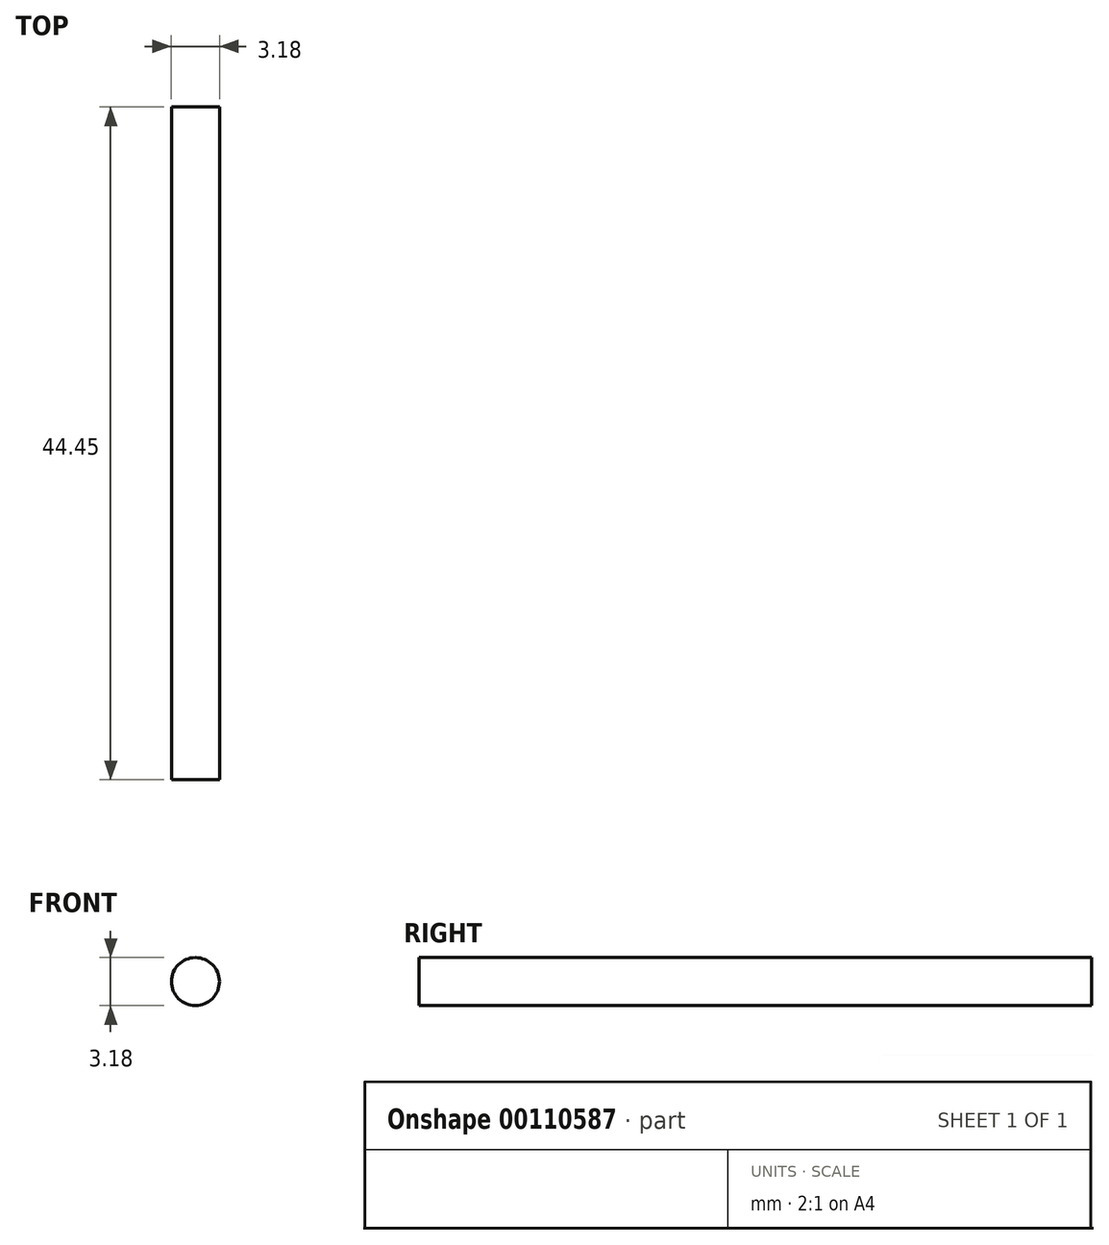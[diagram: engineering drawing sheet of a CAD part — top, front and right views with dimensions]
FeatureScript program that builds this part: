
annotation { "Feature Type Name" : "Feature", "Feature Type Description" : "" }
export const myFeature = defineFeature(function(context is Context, id is Id, definition is map)
    precondition{}
    {
        {
            var Q0;
            Q0=qCreatedBy(makeId("Front.planeOp"),FACE);
            var sketch = newSketch(context, id + "F0", { "sketchPlane" : qUnion([Q0])});
            skCircle(sketch, "E0", {"center": v(0, 0) * mm, "radius": 1.59 * mm});
            skSolve(sketch);
        }
        {
            var Q0;
            Q0=makeQuery(id+"F0.imprint","IMPRINT",FACE,{"disambiguationData":[TD([[makeQuery(id+"F0.imprint","IMPRINT",EDGE,{"derivedFrom":sQuery(id+"F0.wireOp",EDGE,"E0")}),1.0]])]});
            extrude(context, id + "F1", {"entities" : qUnion([Q0]), "depth" : 44.45 * mm});
        }
    });
